# Revit family: Mechanical_Menzies-Metal_Built-Up-Roof-Flat-Top-Vent-TPO
name_source: partatom
category: Mechanical Equipment
revit_build: Autodesk Revit 2018 (Build: 20170223_1515(x64)
units: mm (PartAtom-declared; Revit-internal decimal feet)

## family parameters
Cut with Voids When Loaded = No
Host = Face
OmniClass Number = 23.70.50.21.24.11
OmniClass Title = Roof Waste Water Drains
Part Type = Normal
Room Calculation Point = No
Round Connector Dimension = Use Diameter
Shared = No

## types (1)
- 14 x 14
    Assembly Code = D2040200
    CW Connection = No
    Default Elevation = 48 "
    Depth = 14 "
    Description = Built Up Roof Flat Top Vent TPO
    Drain Flow = 0 GPM
    Edition number = 1
    HW Connection = No
    Manufacturer = Menzies Metal Products
    Model = 600-2142TPO
    Product Guid = 2799f1e7-5a87-41a4-ae29-f83a5cfc54c4
    Product Material = Metal - Menzies Metal Products - Aluminium TPO Coated
    Product data url = https://www.bimobject.com
    URL = https://www.menzies-metal.com
    Vent Connection = No
    Waste Connection = No
    Weight = 10.95 lbf
    Width = 14 "

## geometry (parser evidence)
native form markers: Sweep x3
no freeform markers — native parametric forms only
